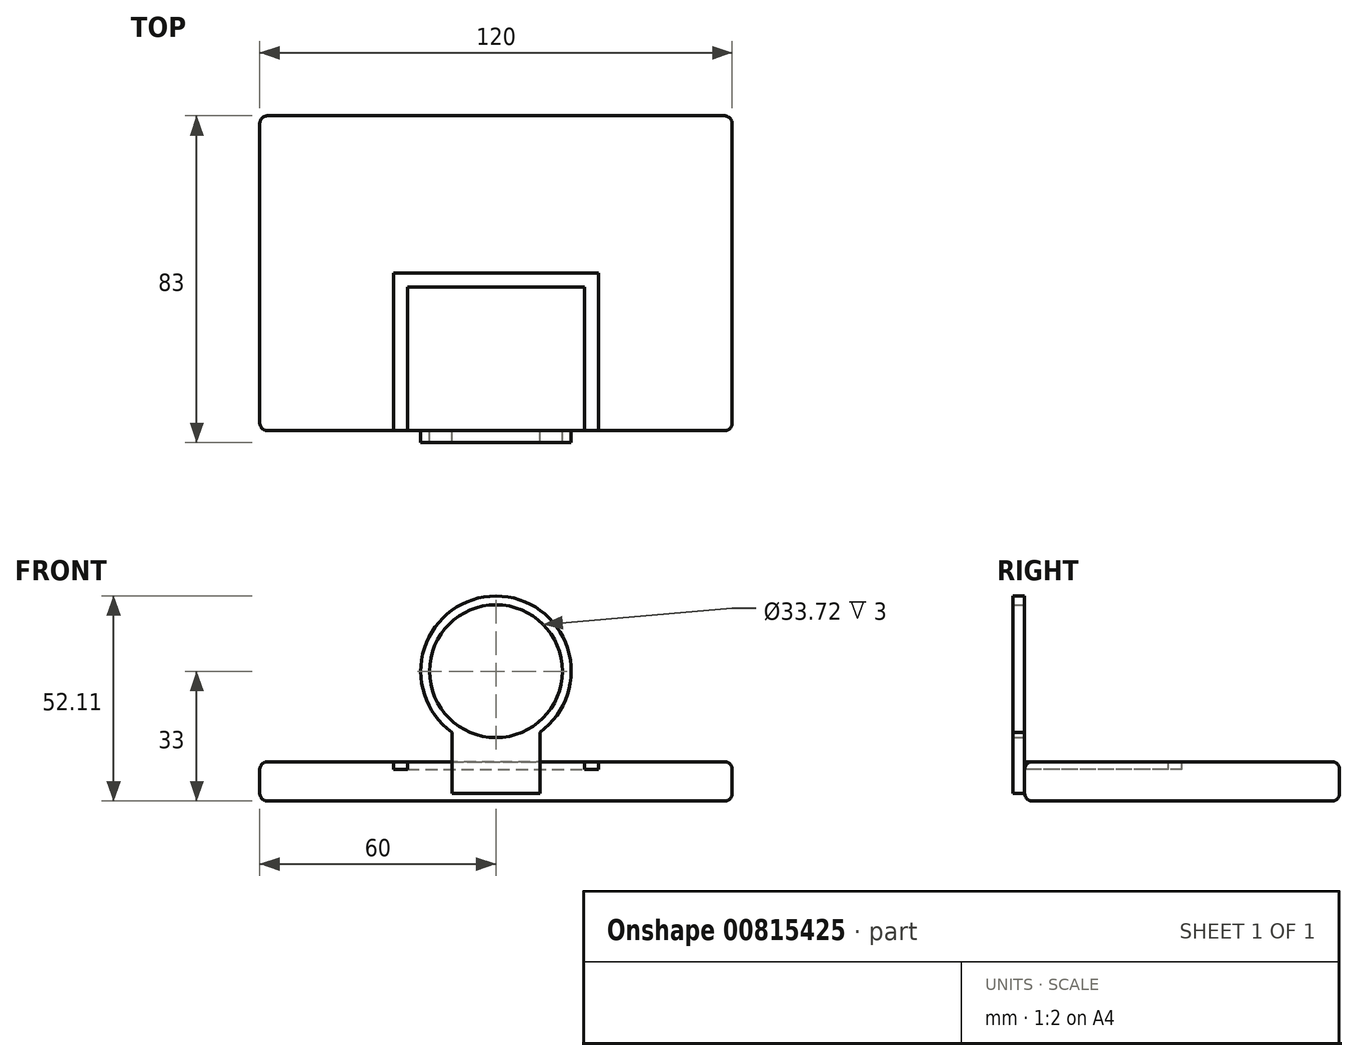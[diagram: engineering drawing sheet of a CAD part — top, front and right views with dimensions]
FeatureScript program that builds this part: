
annotation { "Feature Type Name" : "Feature", "Feature Type Description" : "" }
export const myFeature = defineFeature(function(context is Context, id is Id, definition is map)
    precondition{}
    {
        {
            var Q0;
            Q0=qCreatedBy(makeId("Top.planeOp"),FACE);
            var sketch = newSketch(context, id + "F0", { "sketchPlane" : qUnion([Q0])});
            skLineSegment(sketch, "E0.bottom", {"start": v(-60, 40) * mm, "end": v(60, 40) * mm});
            skLineSegment(sketch, "E0.top", {"start": v(-60, -40) * mm, "end": v(60, -40) * mm});
            skLineSegment(sketch, "E0.left", {"start": v(-60, 40) * mm, "end": v(-60, -40) * mm});
            skLineSegment(sketch, "E0.right", {"start": v(60, 40) * mm, "end": v(60, -40) * mm});
            skPoint(sketch, "E0.middle", {"position": v(0, 0) * mm});
            skLineSegment(sketch, "E1", {"start": v(-22.36, 0) * mm, "end": v(0, 0) * mm});
            skLineSegment(sketch, "E2", {"start": v(22.5, 0) * mm, "end": v(0, 0) * mm});
            skLineSegment(sketch, "E3", {"start": v(-22.36, 0) * mm, "end": v(-22.36, -40) * mm});
            skLineSegment(sketch, "E4", {"start": v(22.5, 0) * mm, "end": v(22.5, -40) * mm});
            skPoint(sketch, "E5.orphan", {"position": v(-60, 0) * mm});
            skPoint(sketch, "E6.orphan", {"position": v(60, 0) * mm});
            skPoint(sketch, "E7.start.orphan", {"position": v(0, -40) * mm});
            skLineSegment(sketch, "E8", {"start": v(-25.86, -40) * mm, "end": v(-25.86, 0) * mm});
            skLineSegment(sketch, "E9", {"start": v(26, -40) * mm, "end": v(26, 0) * mm});
            skLineSegment(sketch, "E10", {"start": v(-25.86, 0) * mm, "end": v(-25.86, 3.5) * mm});
            skLineSegment(sketch, "E11", {"start": v(-25.86, 3.5) * mm, "end": v(26, 3.5) * mm});
            skLineSegment(sketch, "E12", {"start": v(26, 3.5) * mm, "end": v(26, 0) * mm});
            skSolve(sketch);
        }
        {
            var Q0;
            Q0 = qSketchRegion(id + "F0", true);
            extrude(context, id + "F1", {"entities" : qUnion([Q0]), "oppositeDirection" : true, "depth" : 10 * mm, "offsetDistance" : 25 * mm});
        }
        {
            var Q0;
            Q0=makeQuery(id+"F1.opExtrude","CAP_FACE",FACE,{"disambiguationData":[OSD([sQuery(id+"F0.wireOp",EDGE,"E0.bottom"),sQuery(id+"F0.wireOp",EDGE,"E0.top"),sQuery(id+"F0.wireOp",EDGE,"E0.left"),sQuery(id+"F0.wireOp",EDGE,"E0.right")])],"isStart":true});
            var sketch = newSketch(context, id + "F2", { "sketchPlane" : qUnion([Q0])});
            skLineSegment(sketch, "E13", {"start": v(0, 0) * mm, "end": v(0, -40) * mm});
            skLineSegment(sketch, "E14", {"start": v(0, 0) * mm, "end": v(26, 0) * mm});
            skLineSegment(sketch, "E15", {"start": v(26, 0) * mm, "end": v(-26, 0) * mm});
            skLineSegment(sketch, "E16", {"start": v(-26, 0) * mm, "end": v(-26, -40) * mm});
            skLineSegment(sketch, "E17", {"start": v(-22.5, -3.5) * mm, "end": v(-22.5, -40) * mm});
            skLineSegment(sketch, "E18", {"start": v(22.5, -3.5) * mm, "end": v(22.5, -40) * mm});
            skLineSegment(sketch, "E19", {"start": v(26, 0) * mm, "end": v(26, -40) * mm});
            skLineSegment(sketch, "E20", {"start": v(-22.5, -3.5) * mm, "end": v(22.5, -3.5) * mm});
            skPoint(sketch, "E21.orphan", {"position": v(-60, 0) * mm});
            skPoint(sketch, "E22.orphan", {"position": v(22.5, 0) * mm});
            skPoint(sketch, "E23.orphan", {"position": v(-22.5, 0) * mm});
            skPoint(sketch, "E24.orphan", {"position": v(-26, -3.5) * mm});
            skPoint(sketch, "E25.orphan", {"position": v(60, 0) * mm});
            skSolve(sketch);
        }
        {
            var Q0;
            {var subQ0=sQuery(id+"F2.wireOp",EDGE,"E16");Q0=makeQuery(id+"F2.imprint","IMPRINT",FACE,{"disambiguationData":[TD([[makeQuery(id+"F2.imprint","IMPRINT",EDGE,{"derivedFrom":subQ0}),1.0]])]});}
            var Q1;
            {var subQ0=sQuery(id+"F2.wireOp",EDGE,"E18");Q1=makeQuery(id+"F2.imprint","IMPRINT",FACE,{"disambiguationData":[TD([[makeQuery(id+"F2.imprint","IMPRINT",EDGE,{"derivedFrom":subQ0}),1.0]])]});}
            extrude(context, id + "F3", {"entities" : qUnion([Q0, Q1]), "operationType" : NewBodyOperationType.REMOVE, "oppositeDirection" : true, "depth" : 2 * mm, "offsetDistance" : 25 * mm});
        }
        {
            var Q0;
            Q0=makeQuery(id+"F1.opExtrude","CAP_EDGE",EDGE,{"disambiguationData":[OSD([sQuery(id+"F0.wireOp",EDGE,"E0.bottom")])],"isStart":true});
            var Q1;
            Q1=makeQuery(id+"F1.opExtrude","CAP_EDGE",EDGE,{"disambiguationData":[OSD([sQuery(id+"F0.wireOp",EDGE,"E0.left")])],"isStart":true});
            var Q2;
            Q2=makeQuery(id+"F1.opExtrude","CAP_EDGE",EDGE,{"disambiguationData":[OSD([sQuery(id+"F0.wireOp",EDGE,"E0.right")])],"isStart":true});
            var Q3;
            {var subQ0=sQuery(id+"F0.wireOp",EDGE,"E0.right");var subQ1=sQuery(id+"F0.wireOp",EDGE,"E0.top");Q3=makeQuery(id+"F3.boolean.opBoolean","SPLIT",EDGE,{"disambiguationData":[TD([makeQuery(id+"F1.opExtrude","SWEPT_FACE",FACE,{"disambiguationData":[OSD([subQ0])]})])],"derivedFrom":makeQuery(id+"F1.opExtrude","CAP_EDGE",EDGE,{"disambiguationData":[OSD([subQ1])],"isStart":true})});}
            var Q4;
            {var subQ0=sQuery(id+"F0.wireOp",EDGE,"E0.left");var subQ1=sQuery(id+"F0.wireOp",EDGE,"E0.top");Q4=makeQuery(id+"F3.boolean.opBoolean","SPLIT",EDGE,{"disambiguationData":[TD([makeQuery(id+"F1.opExtrude","SWEPT_FACE",FACE,{"disambiguationData":[OSD([subQ0])]})])],"derivedFrom":makeQuery(id+"F1.opExtrude","CAP_EDGE",EDGE,{"disambiguationData":[OSD([subQ1])],"isStart":true})});}
            var Q5;
            Q5=makeQuery(id+"F1.opExtrude","SWEPT_EDGE",EDGE,{"disambiguationData":[OSD([sQuery(id+"F0.wireOp",EDGE,"E0.top"),sQuery(id+"F0.wireOp",EDGE,"E0.right")])]});
            var Q6;
            Q6=makeQuery(id+"F1.opExtrude","CAP_EDGE",EDGE,{"disambiguationData":[OSD([sQuery(id+"F0.wireOp",EDGE,"E0.right")])],"isStart":false});
            var Q7;
            Q7=makeQuery(id+"F1.opExtrude","SWEPT_EDGE",EDGE,{"disambiguationData":[OSD([sQuery(id+"F0.wireOp",EDGE,"E0.bottom"),sQuery(id+"F0.wireOp",EDGE,"E0.right")])]});
            var Q8;
            Q8=makeQuery(id+"F1.opExtrude","CAP_EDGE",EDGE,{"disambiguationData":[OSD([sQuery(id+"F0.wireOp",EDGE,"E0.bottom")])],"isStart":false});
            var Q9;
            Q9=makeQuery(id+"F1.opExtrude","SWEPT_EDGE",EDGE,{"disambiguationData":[OSD([sQuery(id+"F0.wireOp",EDGE,"E0.bottom"),sQuery(id+"F0.wireOp",EDGE,"E0.left")])]});
            var Q10;
            Q10=makeQuery(id+"F1.opExtrude","CAP_EDGE",EDGE,{"disambiguationData":[OSD([sQuery(id+"F0.wireOp",EDGE,"E0.left")])],"isStart":false});
            var Q11;
            Q11=makeQuery(id+"F1.opExtrude","CAP_EDGE",EDGE,{"disambiguationData":[OSD([sQuery(id+"F0.wireOp",EDGE,"E0.top")])],"isStart":false});
            var Q12;
            Q12=makeQuery(id+"F1.opExtrude","SWEPT_EDGE",EDGE,{"disambiguationData":[OSD([sQuery(id+"F0.wireOp",EDGE,"E0.top"),sQuery(id+"F0.wireOp",EDGE,"E0.left")])]});
            fillet(context, id + "F4", {"entities" : qUnion([Q0, Q1, Q2, Q3, Q4, Q5, Q6, Q7, Q8, Q9, Q10, Q11, Q12]), "radius" : 2 * mm, "tangentPropagation" : true, "allowEdgeOverflow" : false});
        }
        {
            var Q0;
            Q0=makeQuery(id+"F1.opExtrude","SWEPT_FACE",FACE,{"disambiguationData":[OSD([sQuery(id+"F0.wireOp",EDGE,"E0.top")])]});
            var sketch = newSketch(context, id + "F5", { "sketchPlane" : qUnion([Q0])});
            skPoint(sketch, "E26", {"position": v(0, 0) * mm});
            skCircle(sketch, "E27", {"center": v(0, 23) * mm, "radius": 19.11 * mm});
            skLineSegment(sketch, "E28.left", {"start": v(-11.18, 7.5) * mm, "end": v(-11.18, 0) * mm});
            skLineSegment(sketch, "E28.right", {"start": v(11.18, 7.5) * mm, "end": v(11.18, 0) * mm});
            skLineSegment(sketch, "E29", {"start": v(0, 0) * mm, "end": v(-11.18, 0) * mm});
            skLineSegment(sketch, "E30", {"start": v(-11.18, 0) * mm, "end": v(11.18, 0) * mm});
            skCircle(sketch, "E31", {"center": v(0, 23) * mm, "radius": 16.86 * mm});
            skLineSegment(sketch, "E32", {"start": v(11.18, 0) * mm, "end": v(11.18, -8) * mm});
            skPoint(sketch, "E32.endSnap0", {"position": v(0, -8) * mm});
            skLineSegment(sketch, "E33", {"start": v(-11.18, -8) * mm, "end": v(-11.18, 0) * mm});
            skLineSegment(sketch, "E34", {"start": v(-11.18, -8) * mm, "end": v(11.18, -8) * mm});
            skSolve(sketch);
        }
        {
            var Q0;
            {var subQ1=sQuery(id+"F5.wireOp",EDGE,"E28.left");Q0=makeQuery(id+"F5.imprint","IMPRINT",FACE,{"disambiguationData":[TD([[makeQuery(id+"F5.imprint","IMPRINT",EDGE,{"derivedFrom":subQ1}),1.0]])]});}
            var Q1;
            {var subQ0=sQuery(id+"F5.wireOp",EDGE,"E27");var subQ1=makeQuery(id+"F5.imprint","INTERSECT",VERTEX,{"derivedFrom":[subQ0,sQuery(id+"F5.wireOp",EDGE,"E28.left")]});Q1=makeQuery(id+"F5.imprint","IMPRINT",FACE,{"disambiguationData":[TD([[makeQuery(id+"F5.imprint","IMPRINT",EDGE,{"disambiguationData":[TD([[subQ1,-1.0]])],"derivedFrom":subQ0}),1.0]])]});}
            var Q2;
            {var subQ1=sQuery(id+"F5.wireOp",EDGE,"E32");Q2=makeQuery(id+"F5.imprint","IMPRINT",FACE,{"disambiguationData":[TD([[makeQuery(id+"F5.imprint","IMPRINT",EDGE,{"derivedFrom":subQ1}),-1.0]])]});}
            extrude(context, id + "F6", {"entities" : qUnion([Q0, Q1, Q2]), "depth" : 3 * mm, "offsetDistance" : 25 * mm});
        }
    });
